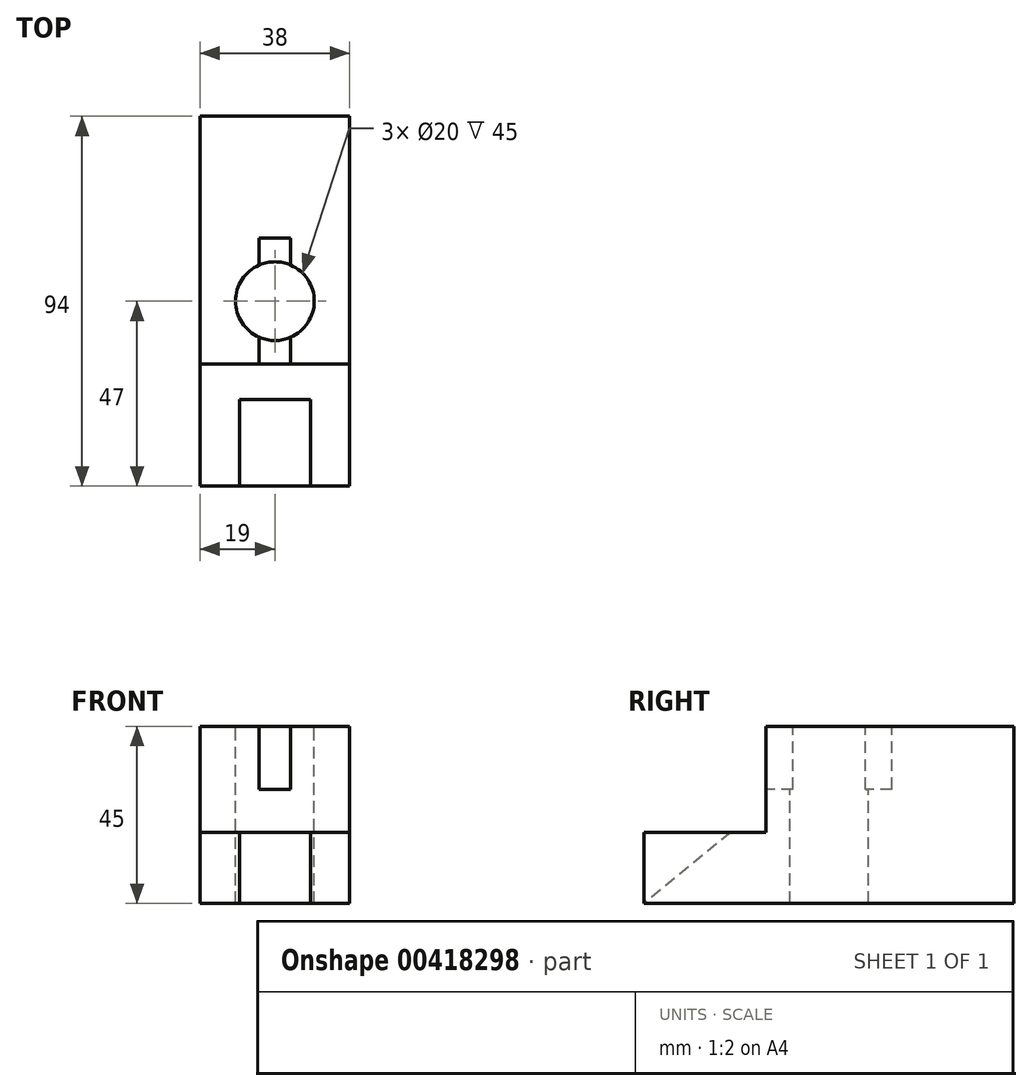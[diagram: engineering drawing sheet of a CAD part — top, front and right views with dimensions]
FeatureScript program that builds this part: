
annotation { "Feature Type Name" : "Feature", "Feature Type Description" : "" }
export const myFeature = defineFeature(function(context is Context, id is Id, definition is map)
    precondition{}
    {
        {
            var Q0;
            Q0=qCreatedBy(makeId("Right.planeOp"),FACE);
            var sketch = newSketch(context, id + "F0", { "sketchPlane" : qUnion([Q0])});
            skLineSegment(sketch, "E0.bottom", {"start": v(-47, 22.5) * mm, "end": v(47, 22.5) * mm});
            skLineSegment(sketch, "E0.top", {"start": v(-47, -22.5) * mm, "end": v(47, -22.5) * mm});
            skLineSegment(sketch, "E0.left", {"start": v(-47, 22.5) * mm, "end": v(-47, -22.5) * mm});
            skLineSegment(sketch, "E0.right", {"start": v(47, 22.5) * mm, "end": v(47, -22.5) * mm});
            skPoint(sketch, "E0.middle", {"position": v(0, 0) * mm});
            skSolve(sketch);
        }
        {
            var Q0;
            Q0 = qSketchRegion(id + "F0", true);
            extrude(context, id + "F1", {"entities" : qUnion([Q0]), "endBound" : BoundingType.SYMMETRIC, "depth" : 38 * mm});
        }
        {
            var Q0;
            Q0=makeQuery(id+"F1.opExtrude","CAP_FACE",FACE,{"disambiguationData":[OSD([sQuery(id+"F0.wireOp",EDGE,"E0.bottom"),sQuery(id+"F0.wireOp",EDGE,"E0.top"),sQuery(id+"F0.wireOp",EDGE,"E0.left"),sQuery(id+"F0.wireOp",EDGE,"E0.right")])],"isStart":false});
            var sketch = newSketch(context, id + "F2", { "sketchPlane" : qUnion([Q0])});
            skLineSegment(sketch, "E1.bottom", {"start": v(-47, 22.5) * mm, "end": v(-16, 22.5) * mm});
            skLineSegment(sketch, "E1.top", {"start": v(-47, -4.5) * mm, "end": v(-16, -4.5) * mm});
            skLineSegment(sketch, "E1.left", {"start": v(-47, 22.5) * mm, "end": v(-47, -4.5) * mm});
            skLineSegment(sketch, "E1.right", {"start": v(-16, 22.5) * mm, "end": v(-16, -4.5) * mm});
            skSolve(sketch);
        }
        {
            var Q0;
            Q0 = qSketchRegion(id + "F2", true);
            extrude(context, id + "F3", {"entities" : qUnion([Q0]), "operationType" : NewBodyOperationType.REMOVE, "endBound" : BoundingType.THROUGH_ALL, "oppositeDirection" : true, "depth" : 25 * mm});
        }
        {
            var Q0;
            Q0=makeQuery(id+"F1.opExtrude","SWEPT_FACE",FACE,{"disambiguationData":[OSD([sQuery(id+"F0.wireOp",EDGE,"E0.bottom")])]});
            var sketch = newSketch(context, id + "F4", { "sketchPlane" : qUnion([Q0])});
            skCircle(sketch, "E2", {"center": v(0, 0) * mm, "radius": 10 * mm});
            skSolve(sketch);
        }
        {
            var Q0;
            Q0 = qSketchRegion(id + "F4", true);
            extrude(context, id + "F5", {"entities" : qUnion([Q0]), "operationType" : NewBodyOperationType.REMOVE, "endBound" : BoundingType.THROUGH_ALL, "oppositeDirection" : true, "depth" : 25 * mm});
        }
        {
            var Q0;
            Q0=makeQuery(id+"F1.opExtrude","SWEPT_FACE",FACE,{"disambiguationData":[OSD([sQuery(id+"F0.wireOp",EDGE,"E0.bottom")])]});
            var sketch = newSketch(context, id + "F6", { "sketchPlane" : qUnion([Q0])});
            skLineSegment(sketch, "E3.bottom", {"start": v(-4, 16) * mm, "end": v(4, 16) * mm});
            skLineSegment(sketch, "E3.top", {"start": v(-4, -16) * mm, "end": v(4, -16) * mm});
            skLineSegment(sketch, "E3.left", {"start": v(-4, 16) * mm, "end": v(-4, -16) * mm});
            skLineSegment(sketch, "E3.right", {"start": v(4, 16) * mm, "end": v(4, -16) * mm});
            skSolve(sketch);
        }
        {
            var Q0;
            Q0 = qSketchRegion(id + "F6", true);
            extrude(context, id + "F7", {"entities" : qUnion([Q0]), "operationType" : NewBodyOperationType.REMOVE, "oppositeDirection" : true, "depth" : 16 * mm});
        }
        {
            var Q0;
            Q0=qCreatedBy(makeId("Right.planeOp"),FACE);
            var sketch = newSketch(context, id + "F8", { "sketchPlane" : qUnion([Q0])});
            skLineSegment(sketch, "E4", {"start": v(-47, -4.5) * mm, "end": v(-25, -4.5) * mm});
            skLineSegment(sketch, "E5", {"start": v(-25, -4.5) * mm, "end": v(-47, -22.5) * mm});
            skLineSegment(sketch, "E6", {"start": v(-47, -22.5) * mm, "end": v(-47, -4.5) * mm});
            skSolve(sketch);
        }
        {
            var Q0;
            Q0 = qSketchRegion(id + "F8", true);
            extrude(context, id + "F9", {"entities" : qUnion([Q0]), "operationType" : NewBodyOperationType.REMOVE, "endBound" : BoundingType.SYMMETRIC, "oppositeDirection" : true, "depth" : 18 * mm});
        }
    });
